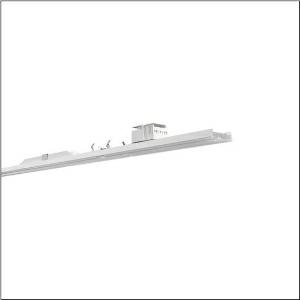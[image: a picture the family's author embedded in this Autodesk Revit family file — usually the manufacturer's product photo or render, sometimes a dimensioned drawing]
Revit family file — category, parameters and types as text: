
# Revit family: licross_r__11_recessed_mo_51tl14dn485f_5601
name_source: partatom
category: Lighting Fixtures
units: mm (PartAtom-declared; Revit-internal decimal feet)

## family parameters
Cut with Voids When Loaded = No
Host = Face
Light Source = No
Part Type = Normal
Room Calculation Point = No
Round Connector Dimension = Use Diameter
Shared = No

## types (1)
- --- (1 x LED, 8550 lm, 56.2 W, 4000K)
    Apparent Load = 56 VA
    CIE Flux Codes = 56 84 97 100 100
    Color Rendering = 80
    Color Temperature = 4000K
    Default Elevation = 1800 mm
    Description = Licross® 11 Recessed MOluminaire insert, length: 1.500mm, width: 66mm, height: 67mm, LED rated luminous flux: 8.550lm, light colour: 840, control gear: DALI 2, control gear: ECG DALI, with plug, 5-pole, with phase selection, mains connection: 220..240V, AC, 50/60Hz, halogen-free wiring, primary optical cover: cover, of PMMA, light emission: direct distribution, primary light characteristic: asymmetric, protection rating (complete): IP40, insulation class (complete): insulation class I (protective earthing), certification: CE, ENEC, VDE, protection symbol: D if used in an environment without relevant dust loads with corresponding accessories, permissible ambient temperature for indoor applications: -25..+35°C, reducing of maximum allowable ambient temperature of 5°C with ceiling mounting, corresponds to IFS (International Featured Standards) requirements for safety and quality in the food industry, packaging unit: 1 piece
    Height = 58 mm
    Lamp = 1 x LED
    Lamp Light Flux = 8550 lm
    Lamp Power = 56.2 W
    Lamp count = 1
    Length = 1500 mm
    Luminous efficacy = 152 lm/W
    Manufacturer = Siteco
    ModVariant = No
    Model = 51TL14DN485F
    Mounting Place = Ceiling
    Mounting Type = Pendant
    Number of Poles = 1
    OnlyDefault = Yes
    Power Factor = 1
    Product Name = Licross® 11 Recessed MO
    Product group = luminaire insert
    ProductGroupID = 902
    Protection Class = Protection class I
    Protection Degree = IP 40
    RLX_Detail_Level = 1
    RlxData = <blob elided: 22733 chars, md5=0125525b>
    Socket = socket
    Standby Power = 0 W
    System Light Flux = 8550 lm
    System Power = 56 W
    Type Comments = factory setting: luminous flux: 100 % | dim-lin: 254 | 370 mA
    Type Image = l_1266722.jpg
    URL = http://relux.com
    VarID = @adj_138863
    Voltage = 0 V
    Weight = 0.00 kg
    Width = 66 mm

## geometry (parser evidence)
native form markers: Blend x4, Sweep x12
no freeform markers — native parametric forms only
